# Revit family: Pressure_Reducing_Valve-Zurn_Wilkins-Model_NR3XLC_Threaded_(12-2_Inch)
name_source: partatom
category: Pipe Accessories
units: mm (PartAtom-declared; Revit-internal decimal feet)

## family parameters
Always vertical = Yes
Cut with Voids When Loaded = No
OmniClass Number = 23.65.55.14.17
OmniClass Title = Adjusting/Controlling Valves for Liquid Services
Part Type = Valve - Breaks Into
Round Connector Dimension = Use Radius
Shared = No
Work Plane-Based = No

## types (6) — shared parameters
Assembly Code = D2020300
Date of publishing = 2/1/2012
Default Elevation = 0' - 0"
Description = Water Pressure Reducing Valve with Integral By-pass check Valve and Strainer
Design country = United States
Edition number = 1
Factory Preset Pressure = 50.00 psi
Flow Rate (GPM) = 0 GPM
Main Material = Paint - Zurn - Bronze
Manufacturer = Zurn Water, LLC
Manufacturer Brand = Zurn Wilkins
Manufacturer country = United States
Manufacturer name = Zurn Wilkins
Max Working Water Temperature = 140 °F
Model = NR3XLC
Modified Data = 08/4/2025
Nominal height = 0' - 0"
Nominal width = 0' - 0"
Product Documentation Link = https://files.zurn.com
Product Installation Sheet URL = https://files.zurn.com
Product Page URL = https://www.zurn.com
Product SKU = zurn-nr3xl
Product data URL = http://bimobject.com
Product family = Adjusting/Controlling Valves for Liquid Services
Product group = Water Pressure Reducing Valves
QR code = http://bimobject.com
Repair Parts URL = https://files.zurn.com
URL = https://www.zurn.com
Weight Net (Kg) = 0
Width = 0' - 0"

## per-type parameters (varying)
- 2-NR3XLC (2" NR3XLC): Bell Base Length=0' - 0 1/4"; Bell Base Radius=0' - 1 21/32"; Bell Blend Radius=0' - 1 1/4"; Bell Hex Radius=0' - 1 1/4"; Bell Upper Base Length=0' - 2 1/32"; Bell Upper Base Radius=0' - 1 1/4"; Body Base Tail Radius=0' - 1 3/16"; Body Radius=0' - 1 7/16"; Body Seat Bell Length=0' - 1"; Body Tail Radius=0' - 0 7/16"; Body Thread Radius=0' - 1 5/8"; Body Top Length=0' - 1 23/32"; Body Top Radius=0' - 1 7/16"; Body Top Seat Bell Radius=0' - 1 7/8"; Body Width=0' - 0 17/32"; DIM A - Length=0' - 6 1/4"; DIM B - Height=0' - 8 1/2"; DIM C - Body Center to Tail Length=0' - 2"; DIM D - BELL DIAMETER=0' - 3 3/4"; Length=0' - 5"; Max Working Water Pressure=300.00 psi; Nominal Diameter=0' - 2"; Nominal Radius=0' - 1"; Nut Diameter=0' - 4"; Nut Length=0' - 3"; Nut Size=Nut : 2 inch; Nut Width=0' - 0 7/8"; Polygon diameter=0' - 2 1/4"; Product Weight (lbs)=8; Reduced Pressure Range=25 to 75 psi; Tail piece diameter=0' - 2 21/32"; Tailpiece radius=0' - 1 11/32"
- 112-NR3XLC (1 1/2" NR3XLC): Bell Base Length=0' - 0 1/4"; Bell Base Radius=0' - 1 21/32"; Bell Blend Radius=0' - 1 1/4"; Bell Hex Radius=0' - 1 1/4"; Bell Upper Base Length=0' - 2 1/32"; Bell Upper Base Radius=0' - 1 1/4"; Body Base Tail Radius=0' - 1 3/16"; Body Radius=0' - 1 3/16"; Body Seat Bell Length=0' - 1"; Body Tail Radius=0' - 0 7/16"; Body Thread Radius=0' - 1 11/32"; Body Top Length=0' - 1 25/32"; Body Top Radius=0' - 1 7/16"; Body Top Seat Bell Radius=0' - 1 7/8"; Body Width=0' - 0 13/32"; DIM A - Length=0' - 6 5/16"; DIM B - Height=0' - 8 1/2"; DIM C - Body Center to Tail Length=0' - 1 3/4"; DIM D - BELL DIAMETER=0' - 3 3/4"; Length=0' - 5"; Max Working Water Pressure=300.00 psi; Nominal Diameter=0' - 1 1/2"; Nominal Radius=0' - 0 3/4"; Nut Diameter=0' - 3 3/8"; Nut Length=0' - 3 1/8"; Nut Size=Nut : 1 1/2 inch; Nut Width=0' - 0 7/8"; Polygon diameter=0' - 2 1/4"; Product Weight (lbs)=7; Reduced Pressure Range=25 to 75 psi; Tail piece diameter=0' - 2"; Tailpiece radius=0' - 1"
- 114-NR3XLC (1 1/4" NR3XLC): Bell Base Length=0' - 0 3/16"; Bell Base Radius=0' - 1 3/8"; Bell Blend Radius=0' - 0 7/8"; Bell Hex Radius=0' - 0 31/32"; Bell Upper Base Length=0' - 2 1/32"; Bell Upper Base Radius=0' - 1"; Body Base Tail Radius=0' - 0 13/16"; Body Radius=0' - 1"; Body Seat Bell Length=0' - 0 7/8"; Body Tail Radius=0' - 0 7/16"; Body Thread Radius=0' - 1 3/32"; Body Top Length=0' - 1 3/8"; Body Top Radius=0' - 1 7/32"; Body Top Seat Bell Radius=0' - 1 1/2"; Body Width=0' - 0 7/16"; DIM A - Length=0' - 6 3/16"; DIM B - Height=0' - 7 3/4"; DIM C - Body Center to Tail Length=0' - 1 3/16"; DIM D - BELL DIAMETER=0' - 3"; Length=0' - 5"; Max Working Water Pressure=400.00 psi; Nominal Diameter=0' - 1 1/4"; Nominal Radius=0' - 0 5/8"; Nut Diameter=0' - 3"; Nut Length=0' - 2 7/8"; Nut Size=Nut : 1 1/4 inch; Nut Width=0' - 0 11/16"; Polygon diameter=0' - 2 1/4"; Product Weight (lbs)=6; Reduced Pressure Range=15 to 75 psi; Tail piece diameter=0' - 1 25/32"; Tailpiece radius=0' - 0 29/32"
- 1-NR3XLC (1" NR3XLC): Bell Base Length=0' - 0 3/16"; Bell Base Radius=0' - 1 1/32"; Bell Blend Radius=0' - 0 3/4"; Bell Hex Radius=0' - 0 13/16"; Bell Upper Base Length=0' - 1 3/16"; Bell Upper Base Radius=0' - 0 7/8"; Body Base Tail Radius=0' - 0 13/16"; Body Radius=0' - 0 27/32"; Body Seat Bell Length=0' - 0 15/32"; Body Tail Radius=0' - 0 7/16"; Body Thread Radius=0' - 0 7/8"; Body Top Length=0' - 1 5/32"; Body Top Radius=0' - 1"; Body Top Seat Bell Radius=0' - 1 1/4"; Body Width=0' - 0 17/32"; DIM A - Length=0' - 4 15/16"; DIM B - Height=0' - 6 1/4"; DIM C - Body Center to Tail Length=0' - 1 1/8"; DIM D - BELL DIAMETER=0' - 2 1/2"; Length=0' - 4"; Max Working Water Pressure=400.00 psi; Nominal Diameter=0' - 1"; Nominal Radius=0' - 0 1/2"; Nut Diameter=0' - 2"; Nut Length=0' - 2 1/4"; Nut Size=Nut : 1 inch; Nut Width=0' - 0 21/32"; Polygon diameter=0' - 2 1/4"; Product Weight (lbs)=4; Reduced Pressure Range=15 to 75 psi; Tail piece diameter=0' - 1 1/2"; Tailpiece radius=0' - 0 3/4"
- 34-NR3XLC (3/4" NR3XLC): Bell Base Length=0' - 0 3/16"; Bell Base Radius=0' - 1 1/32"; Bell Blend Radius=0' - 0 3/4"; Bell Hex Radius=0' - 0 13/16"; Bell Upper Base Length=0' - 1 3/16"; Bell Upper Base Radius=0' - 0 7/8"; Body Base Tail Radius=0' - 0 5/8"; Body Radius=0' - 0 11/16"; Body Seat Bell Length=0' - 0 1/2"; Body Tail Radius=0' - 0 11/32"; Body Thread Radius=0' - 0 13/16"; Body Top Length=0' - 1 5/32"; Body Top Radius=0' - 1 1/16"; Body Top Seat Bell Radius=0' - 1 1/4"; Body Width=0' - 0 3/8"; DIM A - Length=0' - 4 7/16"; DIM B - Height=0' - 6 1/4"; DIM C - Body Center to Tail Length=0' - 1 1/8"; DIM D - BELL DIAMETER=0' - 2 1/2"; Length=0' - 3 1/2"; Max Working Water Pressure=400.00 psi; Nominal Diameter=0' - 0 3/4"; Nominal Radius=0' - 0 3/8"; Nut Diameter=0' - 1 3/4"; Nut Length=0' - 2 1/8"; Nut Size=Nut : 3/4 inch; Nut Width=0' - 0 5/8"; Polygon diameter=0' - 2 1/4"; Product Weight (lbs)=3; Reduced Pressure Range=15 to 75 psi; Tail piece diameter=0' - 1 1/4"; Tailpiece radius=0' - 0 5/8"
- 12-NR3XLC (1/2" NR3XLC): Bell Base Length=0' - 0 3/16"; Bell Base Radius=0' - 1 1/32"; Bell Blend Radius=0' - 0 3/4"; Bell Hex Radius=0' - 0 13/16"; Bell Upper Base Length=0' - 1 3/16"; Bell Upper Base Radius=0' - 0 7/8"; Body Base Tail Radius=0' - 0 5/8"; Body Radius=0' - 0 11/16"; Body Seat Bell Length=0' - 0 15/32"; Body Tail Radius=0' - 0 7/16"; Body Thread Radius=0' - 0 13/16"; Body Top Length=0' - 1 5/32"; Body Top Radius=0' - 1 1/16"; Body Top Seat Bell Radius=0' - 1 1/4"; Body Width=0' - 0 7/16"; DIM A - Length=0' - 4 3/8"; DIM B - Height=0' - 6 1/4"; DIM C - Body Center to Tail Length=0' - 1 1/8"; DIM D - BELL DIAMETER=0' - 2 1/2"; Length=0' - 3 1/2"; Max Working Water Pressure=400.00 psi; Nominal Diameter=0' - 0 1/2"; Nominal Radius=0' - 0 1/4"; Nut Diameter=0' - 1 3/4"; Nut Length=0' - 2 1/16"; Nut Size=Nut : 1/2 inch; Nut Width=0' - 0 5/8"; Polygon diameter=0' - 1 3/4"; Product Weight (lbs)=3; Reduced Pressure Range=15 to 75 psi; Tail piece diameter=0' - 1 1/4"; Tailpiece radius=0' - 0 5/8"

## geometry (parser evidence)
native form markers: Blend x1, Sweep x6
no freeform markers — native parametric forms only
